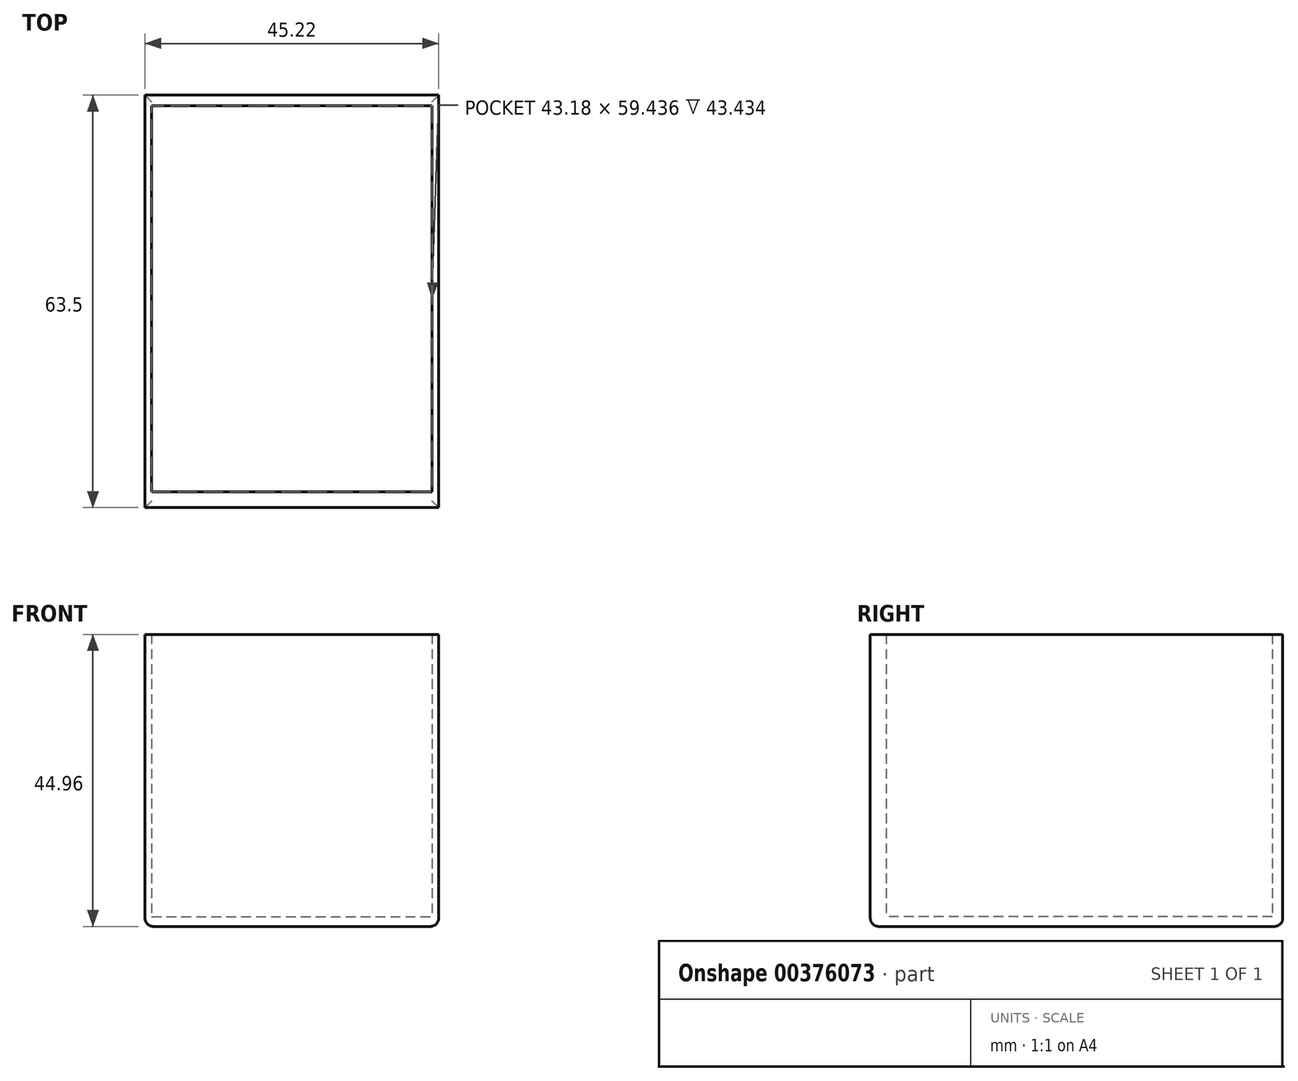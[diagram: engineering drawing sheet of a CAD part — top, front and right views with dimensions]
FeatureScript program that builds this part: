
annotation { "Feature Type Name" : "Feature", "Feature Type Description" : "" }
export const myFeature = defineFeature(function(context is Context, id is Id, definition is map)
    precondition{}
    {
        {
            var Q0;
            Q0=qCreatedBy(makeId("Top.planeOp"),FACE);
            var sketch = newSketch(context, id + "F0", { "sketchPlane" : qUnion([Q0])});
            skLineSegment(sketch, "E0.bottom", {"start": v(-22.6, 31.75) * mm, "end": v(22.6, 31.75) * mm});
            skLineSegment(sketch, "E0.top", {"start": v(-22.6, -31.75) * mm, "end": v(22.6, -31.75) * mm});
            skLineSegment(sketch, "E0.left", {"start": v(-22.6, 31.75) * mm, "end": v(-22.6, -31.75) * mm});
            skLineSegment(sketch, "E0.right", {"start": v(22.6, 31.75) * mm, "end": v(22.6, -31.75) * mm});
            skPoint(sketch, "E0.middle", {"position": v(0, 0) * mm});
            skSolve(sketch);
        }
        {
            var Q0;
            Q0 = qSketchRegion(id + "F0", true);
            extrude(context, id + "F1", {"entities" : qUnion([Q0]), "depth" : 1.52 * mm});
        }
        {
            var Q0;
            Q0=makeQuery(id+"F1.opExtrude","CAP_FACE",FACE,{"disambiguationData":[OSD([sQuery(id+"F0.wireOp",EDGE,"E0.bottom"),sQuery(id+"F0.wireOp",EDGE,"E0.top"),sQuery(id+"F0.wireOp",EDGE,"E0.left"),sQuery(id+"F0.wireOp",EDGE,"E0.right")])],"isStart":false});
            var sketch = newSketch(context, id + "F2", { "sketchPlane" : qUnion([Q0])});
            skLineSegment(sketch, "E1.bottom", {"start": v(-21.6, 30.13) * mm, "end": v(21.59, 30.13) * mm});
            skLineSegment(sketch, "E1.top", {"start": v(-21.6, -29.3) * mm, "end": v(21.59, -29.3) * mm});
            skLineSegment(sketch, "E1.left", {"start": v(-21.6, 30.13) * mm, "end": v(-21.6, -29.3) * mm});
            skLineSegment(sketch, "E1.right", {"start": v(21.59, 30.13) * mm, "end": v(21.59, -29.3) * mm});
            skPoint(sketch, "E1.middle", {"position": v(0, 0.41) * mm});
            skSolve(sketch);
        }
        {
            var Q0;
            Q0=makeQuery(id+"F2.imprint","IMPRINT",FACE,{"disambiguationData":[TD([[makeQuery(id+"F2.imprint","IMPRINT",EDGE,{"derivedFrom":sQuery(id+"F2.wireOp",EDGE,"E1.bottom")}),1.0]])]});
            extrude(context, id + "F3", {"entities" : qUnion([Q0]), "operationType" : NewBodyOperationType.ADD, "depth" : 43.43 * mm});
        }
        {
            var Q0;
            Q0=makeQuery(id+"F1.opExtrude","CAP_FACE",FACE,{"disambiguationData":[OSD([sQuery(id+"F0.wireOp",EDGE,"E0.bottom"),sQuery(id+"F0.wireOp",EDGE,"E0.top"),sQuery(id+"F0.wireOp",EDGE,"E0.left"),sQuery(id+"F0.wireOp",EDGE,"E0.right")])],"isStart":true});
            fillet(context, id + "F4", {"entities" : qUnion([Q0]), "radius" : 1.27 * mm, "tangentPropagation" : true, "allowEdgeOverflow" : false});
        }
    });
